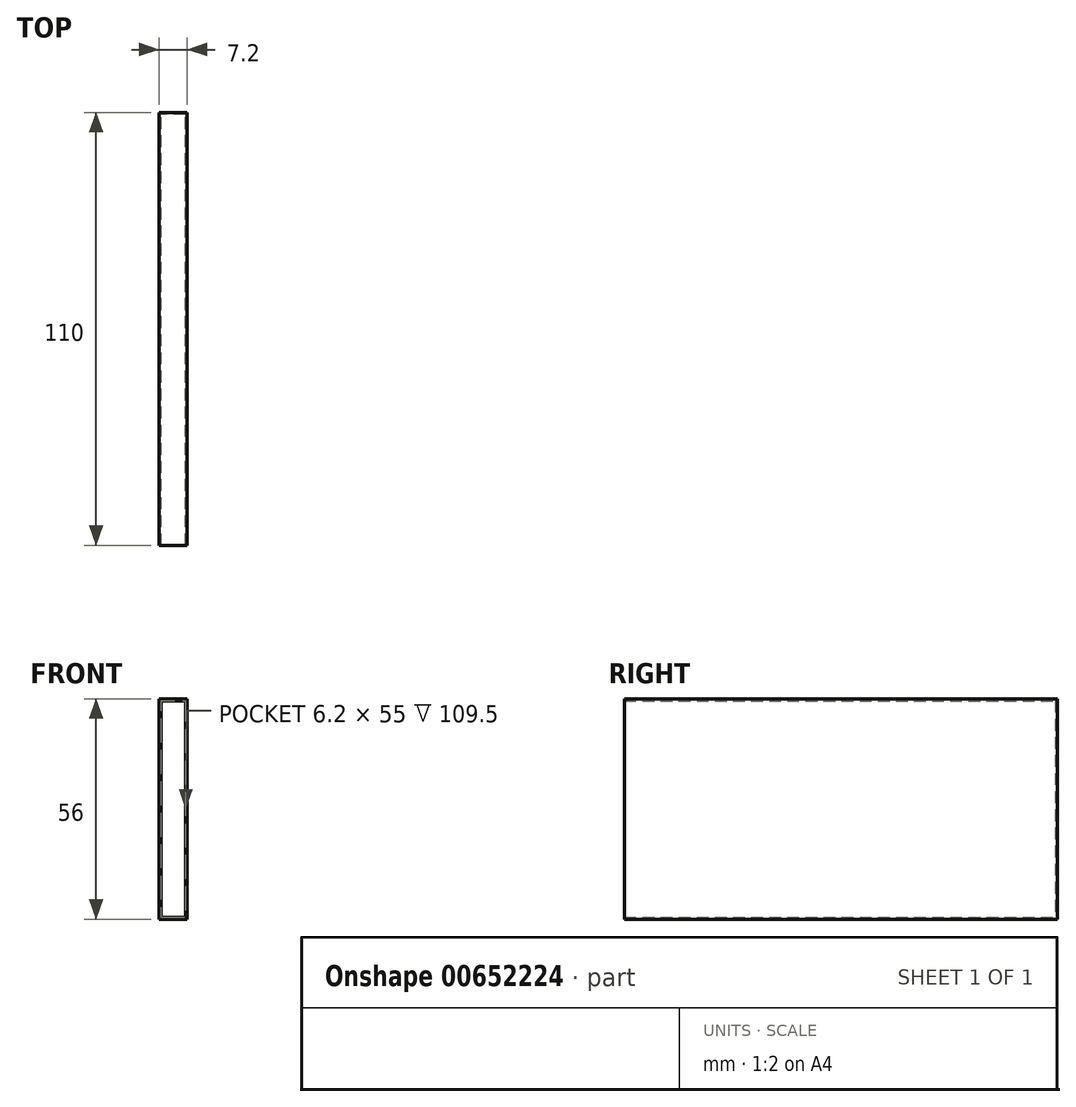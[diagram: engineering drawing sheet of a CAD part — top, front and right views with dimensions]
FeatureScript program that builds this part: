
annotation { "Feature Type Name" : "Feature", "Feature Type Description" : "" }
export const myFeature = defineFeature(function(context is Context, id is Id, definition is map)
    precondition{}
    {
        {
            var Q0;
            Q0=qCreatedBy(makeId("Right.planeOp"),FACE);
            var sketch = newSketch(context, id + "F0", { "sketchPlane" : qUnion([Q0])});
            skLineSegment(sketch, "E0.bottom", {"start": v(-55, 28) * mm, "end": v(55, 28) * mm});
            skLineSegment(sketch, "E0.top", {"start": v(-55, -28) * mm, "end": v(55, -28) * mm});
            skLineSegment(sketch, "E0.left", {"start": v(-55, 28) * mm, "end": v(-55, -28) * mm});
            skLineSegment(sketch, "E0.right", {"start": v(55, 28) * mm, "end": v(55, -28) * mm});
            skPoint(sketch, "E0.middle", {"position": v(0, 0) * mm});
            skSolve(sketch);
        }
        {
            var Q0;
            Q0=makeQuery(id+"F0.imprint","IMPRINT",FACE,{"disambiguationData":[TD([[makeQuery(id+"F0.imprint","IMPRINT",EDGE,{"derivedFrom":sQuery(id+"F0.wireOp",EDGE,"E0.bottom")}),-1.0]])]});
            extrude(context, id + "F1", {"entities" : qUnion([Q0]), "endBound" : BoundingType.SYMMETRIC, "depth" : 7.2 * mm, "offsetDistance" : 25 * mm});
        }
        {
            var Q0;
            Q0=makeQuery(id+"F1.opExtrude","SWEPT_FACE",FACE,{"disambiguationData":[OSD([sQuery(id+"F0.wireOp",EDGE,"E0.left")])]});
            shell(context, id + "F2", {"entities" : qUnion([Q0]), "thickness" : .5 * mm});
        }
    });
